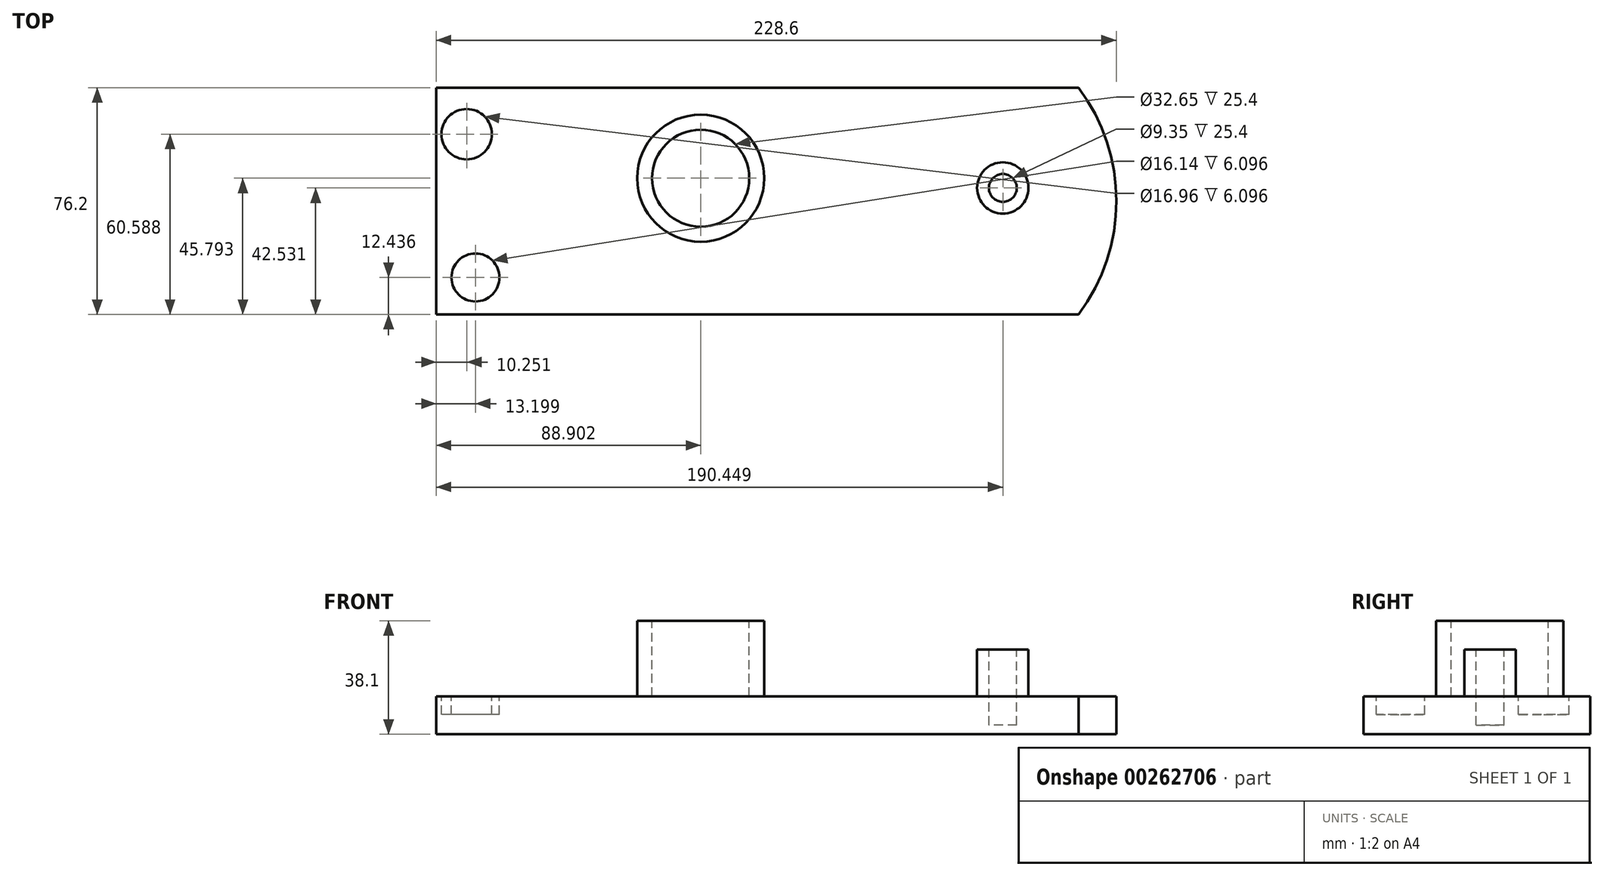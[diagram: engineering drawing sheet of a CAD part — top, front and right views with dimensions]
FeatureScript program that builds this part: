
annotation { "Feature Type Name" : "Feature", "Feature Type Description" : "" }
export const myFeature = defineFeature(function(context is Context, id is Id, definition is map)
    precondition{}
    {
        {
            var Q0;
            Q0=qCreatedBy(makeId("Top.planeOp"),FACE);
            var sketch = newSketch(context, id + "F0", { "sketchPlane" : qUnion([Q0])});
            skLineSegment(sketch, "E0.bottom", {"start": v(-172.83, 44.35) * mm, "end": v(43.07, 44.35) * mm});
            skLineSegment(sketch, "E0.top", {"start": v(-172.83, -31.85) * mm, "end": v(43.07, -31.85) * mm});
            skLineSegment(sketch, "E0.left", {"start": v(-172.83, 44.35) * mm, "end": v(-172.83, -31.85) * mm});
            skArc(sketch, "E1", {"start": v(43.07, -31.85) * mm, "mid": v(55.77, 6.25) * mm, "end": v(43.07, 44.35) * mm});
            skSolve(sketch);
        }
        {
            var Q0;
            Q0 = qSketchRegion(id + "F0", true);
            extrude(context, id + "F1", {"entities" : qUnion([Q0]), "depth" : 12.7 * mm});
        }
        {
            var Q0;
            Q0=makeQuery(id+"F1.opExtrude","CAP_FACE",FACE,{"disambiguationData":[OSD([sQuery(id+"F0.wireOp",EDGE,"E0.bottom"),sQuery(id+"F0.wireOp",EDGE,"E0.top"),sQuery(id+"F0.wireOp",EDGE,"E0.left"),sQuery(id+"F0.wireOp",EDGE,"E1")])],"isStart":false});
            var sketch = newSketch(context, id + "F2", { "sketchPlane" : qUnion([Q0])});
            skCircle(sketch, "E2", {"center": v(-83.93, 13.94) * mm, "radius": 21.35 * mm});
            skSolve(sketch);
        }
        {
            var Q0;
            Q0=makeQuery(id+"F2.imprint","IMPRINT",FACE,{"disambiguationData":[TD([[makeQuery(id+"F2.imprint","IMPRINT",EDGE,{"derivedFrom":sQuery(id+"F2.wireOp",EDGE,"E2")}),-1.0]])]});
            var sketch = newSketch(context, id + "F3", { "sketchPlane" : qUnion([Q0])});
            skCircle(sketch, "E3", {"center": v(17.62, 10.68) * mm, "radius": 8.63 * mm});
            skSolve(sketch);
        }
        {
            var Q0;
            Q0=makeQuery(id+"F3.imprint","IMPRINT",FACE,{"disambiguationData":[TD([[makeQuery(id+"F3.imprint","IMPRINT",EDGE,{"derivedFrom":sQuery(id+"F3.wireOp",EDGE,"E3")}),-1.0]])]});
            var sketch = newSketch(context, id + "F4", { "sketchPlane" : qUnion([Q0])});
            skSolve(sketch);
        }
        {
            var Q0;
            Q0=makeQuery(id+"F2.imprint","IMPRINT",FACE,{"disambiguationData":[TD([[makeQuery(id+"F2.imprint","IMPRINT",EDGE,{"derivedFrom":sQuery(id+"F2.wireOp",EDGE,"E2")}),1.0]])]});
            extrude(context, id + "F5", {"entities" : qUnion([Q0]), "operationType" : NewBodyOperationType.ADD, "depth" : 25.4 * mm});
        }
        {
            var Q0;
            Q0=makeQuery(id+"F3.imprint","IMPRINT",FACE,{"disambiguationData":[TD([[makeQuery(id+"F3.imprint","IMPRINT",EDGE,{"derivedFrom":sQuery(id+"F3.wireOp",EDGE,"E3")}),1.0]])]});
            extrude(context, id + "F6", {"entities" : qUnion([Q0]), "operationType" : NewBodyOperationType.ADD, "depth" : 15.75 * mm});
        }
        {
            var Q0;
            Q0=makeQuery(id+"F5.opExtrude","CAP_FACE",FACE,{"disambiguationData":[OSD([sQuery(id+"F2.wireOp",EDGE,"E2")])],"isStart":false});
            var sketch = newSketch(context, id + "F7", { "sketchPlane" : qUnion([Q0])});
            skCircle(sketch, "E4", {"center": v(-83.93, 13.94) * mm, "radius": 16.33 * mm});
            skSolve(sketch);
        }
        {
            var Q0;
            Q0 = qSketchRegion(id + "F7", true);
            extrude(context, id + "F8", {"entities" : qUnion([Q0]), "operationType" : NewBodyOperationType.REMOVE, "oppositeDirection" : true, "depth" : 25.4 * mm});
        }
        {
            var Q0;
            Q0=makeQuery(id+"F6.opExtrude","CAP_FACE",FACE,{"disambiguationData":[OSD([sQuery(id+"F3.wireOp",EDGE,"E3")])],"isStart":false});
            var sketch = newSketch(context, id + "F9", { "sketchPlane" : qUnion([Q0])});
            skCircle(sketch, "E5", {"center": v(17.62, 10.68) * mm, "radius": 4.67 * mm});
            skSolve(sketch);
        }
        {
            var Q0;
            Q0=makeQuery(id+"F9.imprint","IMPRINT",FACE,{"disambiguationData":[TD([[makeQuery(id+"F9.imprint","IMPRINT",EDGE,{"derivedFrom":sQuery(id+"F9.wireOp",EDGE,"E5")}),1.0]])]});
            extrude(context, id + "F10", {"entities" : qUnion([Q0]), "operationType" : NewBodyOperationType.REMOVE, "oppositeDirection" : true, "depth" : 25.4 * mm});
        }
        {
            var Q0;
            Q0=makeQuery(id+"F4.imprint","IMPRINT",FACE,{"disambiguationData":[TD([[makeQuery(id+"F4.imprint","IMPRINT",EDGE,{"derivedFrom":makeQuery(id+"F3.imprint","IMPRINT",EDGE,{"derivedFrom":sQuery(id+"F3.wireOp",EDGE,"E3")})}),-1.0]])]});
            var sketch = newSketch(context, id + "F11", { "sketchPlane" : qUnion([Q0])});
            skLineSegment(sketch, "E6", {"start": v(-63.2, 21.1) * mm, "end": v(9.24, 11.52) * mm});
            skLineSegment(sketch, "E7", {"start": v(9.24, 11.52) * mm, "end": v(-63.37, 6.57) * mm});
            skSolve(sketch);
        }
        {
            var Q0;
            Q0=makeQuery(id+"F4.imprint","IMPRINT",FACE,{"disambiguationData":[TD([[makeQuery(id+"F4.imprint","IMPRINT",EDGE,{"derivedFrom":makeQuery(id+"F3.imprint","IMPRINT",EDGE,{"derivedFrom":sQuery(id+"F3.wireOp",EDGE,"E3")})}),-1.0]])]});
            var sketch = newSketch(context, id + "F12", { "sketchPlane" : qUnion([Q0])});
            skCircle(sketch, "E8", {"center": v(-159.63, -19.41) * mm, "radius": 8.07 * mm});
            skSolve(sketch);
        }
        {
            var Q0;
            Q0 = qSketchRegion(id + "F12", true);
            extrude(context, id + "F13", {"entities" : qUnion([Q0]), "operationType" : NewBodyOperationType.REMOVE, "oppositeDirection" : true, "depth" : 6.1 * mm});
        }
        {
            var Q0;
            Q0=makeQuery(id+"F4.imprint","IMPRINT",FACE,{"disambiguationData":[TD([[makeQuery(id+"F4.imprint","IMPRINT",EDGE,{"derivedFrom":makeQuery(id+"F3.imprint","IMPRINT",EDGE,{"derivedFrom":sQuery(id+"F3.wireOp",EDGE,"E3")})}),-1.0]])]});
            var sketch = newSketch(context, id + "F14", { "sketchPlane" : qUnion([Q0])});
            skCircle(sketch, "E9", {"center": v(-162.58, 28.74) * mm, "radius": 8.48 * mm});
            skSolve(sketch);
        }
        {
            var Q0;
            Q0 = qSketchRegion(id + "F14", true);
            extrude(context, id + "F15", {"entities" : qUnion([Q0]), "operationType" : NewBodyOperationType.REMOVE, "oppositeDirection" : true, "depth" : 6.1 * mm});
        }
        {
            var Q0;
            Q0=makeQuery(id+"F4.imprint","IMPRINT",FACE,{"disambiguationData":[TD([[makeQuery(id+"F4.imprint","IMPRINT",EDGE,{"derivedFrom":makeQuery(id+"F3.imprint","IMPRINT",EDGE,{"derivedFrom":sQuery(id+"F3.wireOp",EDGE,"E3")})}),-1.0]])]});
            var sketch = newSketch(context, id + "F16", { "sketchPlane" : qUnion([Q0])});
            skCircle(sketch, "E10", {"center": v(-135.28, 29.62) * mm, "radius": 7.74 * mm});
            skCircle(sketch, "E11", {"center": v(-135.28, -19.97) * mm, "radius": 8 * mm});
            skSolve(sketch);
        }
        {
            var Q0;
            Q0 = qSketchRegion(id + "F16", true);
            extrude(context, id + "F17", {"entities" : qUnion([Q0]), "operationType" : NewBodyOperationType.ADD, "oppositeDirection" : true, "depth" : 9.9 * mm});
        }
        {
            var Q0;
            Q0=sQuery(id+"F11.wireOp",EDGE,"E6");
            var Q1;
            Q1=sQuery(id+"F11.wireOp",EDGE,"E7");
            extrude(context, id + "F18", {"bodyType" : ToolBodyType.SURFACE, "surfaceEntities" : qUnion([Q0, Q1]), "depth" : 42.16 * mm});
        }
        {
            var Q0;
            Q0=makeQuery(id+"F18.opExtrude","SWEPT_FACE",FACE,{"disambiguationData":[OSD([sQuery(id+"F11.wireOp",EDGE,"E7")])]});
            var sketch = newSketch(context, id + "F19", { "sketchPlane" : qUnion([Q0])});
            skLineSegment(sketch, "E12", {"start": v(62.77, 41.83) * mm, "end": v(-10, 30.46) * mm});
            skLineSegment(sketch, "E13", {"start": v(-10, 30.46) * mm, "end": v(-10, 54.86) * mm});
            skLineSegment(sketch, "E14", {"start": v(-10, 54.86) * mm, "end": v(62.77, 54.86) * mm});
            skLineSegment(sketch, "E15", {"start": v(62.77, 54.86) * mm, "end": v(62.77, 41.83) * mm});
            skSolve(sketch);
        }
        {
            var Q0;
            Q0 = qSketchRegion(id + "F19", true);
            extrude(context, id + "F20", {"entities" : qUnion([Q0]), "operationType" : NewBodyOperationType.REMOVE, "depth" : 76.2 * mm});
        }
        {
            var Q0;
            Q0=makeQuery(id+"F18.opExtrude","SWEPT_FACE",FACE,{"disambiguationData":[OSD([sQuery(id+"F11.wireOp",EDGE,"E6")])]});
            var sketch = newSketch(context, id + "F21", { "sketchPlane" : qUnion([Q0])});
            skLineSegment(sketch, "E16", {"start": v(-65.43, 54.86) * mm, "end": v(7.65, 28.58) * mm});
            skLineSegment(sketch, "E17", {"start": v(7.65, 28.58) * mm, "end": v(7.65, 54.86) * mm});
            skLineSegment(sketch, "E18", {"start": v(7.65, 54.86) * mm, "end": v(-65.43, 54.86) * mm});
            skSolve(sketch);
        }
        {
            var Q0;
            Q0 = qSketchRegion(id + "F21", true);
            extrude(context, id + "F22", {"entities" : qUnion([Q0]), "operationType" : NewBodyOperationType.REMOVE, "depth" : 54.6 * mm});
        }
    });
